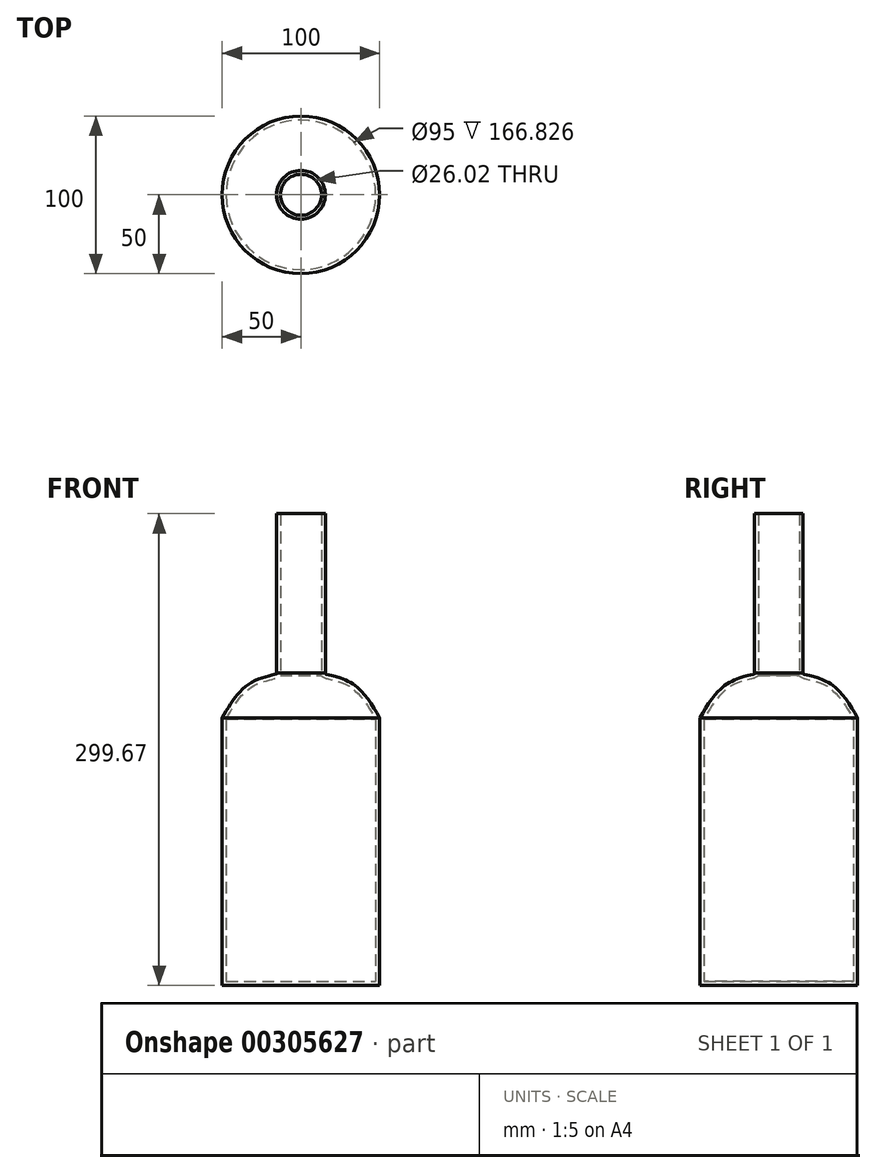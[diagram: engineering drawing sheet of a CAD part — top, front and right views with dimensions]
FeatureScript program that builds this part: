
annotation { "Feature Type Name" : "Feature", "Feature Type Description" : "" }
export const myFeature = defineFeature(function(context is Context, id is Id, definition is map)
    precondition{}
    {
        {
            var Q0;
            Q0=qCreatedBy(makeId("Front.planeOp"),FACE);
            var sketch = newSketch(context, id + "F0", { "sketchPlane" : qUnion([Q0])});
            skLineSegment(sketch, "E0", {"start": v(0, 0) * mm, "end": v(0, 300) * mm});
            skLineSegment(sketch, "E1", {"start": v(0, 0) * mm, "end": v(50, 0) * mm});
            skLineSegment(sketch, "E2", {"start": v(50, 0) * mm, "end": v(50, 170) * mm});
            skFitSpline(sketch, "E3", {"points": [v(50, 170) * mm, v(30.5, 192.89) * mm, v(15.16, 198.12) * mm, v(15.51, 198.47) * mm], "startDerivative": vector(-29.54, 50.83) * mm, "endDerivative": vector(8.7, 4.9) * mm});
            skLineSegment(sketch, "E4", {"start": v(15.51, 198.47) * mm, "end": v(15.51, 299.6) * mm});
            skLineSegment(sketch, "E5", {"start": v(15.51, 299.6) * mm, "end": v(0, 300) * mm});
            skSolve(sketch);
        }
        {
            var Q0;
            Q0 = qSketchRegion(id + "F0", true);
            var Q1;
            Q1=sQuery(id+"F0.wireOp",EDGE,"E0");
            revolve(context, id + "F1", {"entities" : qUnion([Q0]), "axis" : qUnion([Q1]), "revolveType" : RevolveType.FULL});
        }
        {
            var Q0;
            Q0=makeQuery(id+"F1.opRevolve","SWEPT_FACE",FACE,{"disambiguationData":[OSD([sQuery(id+"F0.wireOp",EDGE,"E5")])]});
            shell(context, id + "F2", {"entities" : qUnion([Q0]), "thickness" : 2.5 * mm});
        }
    });
